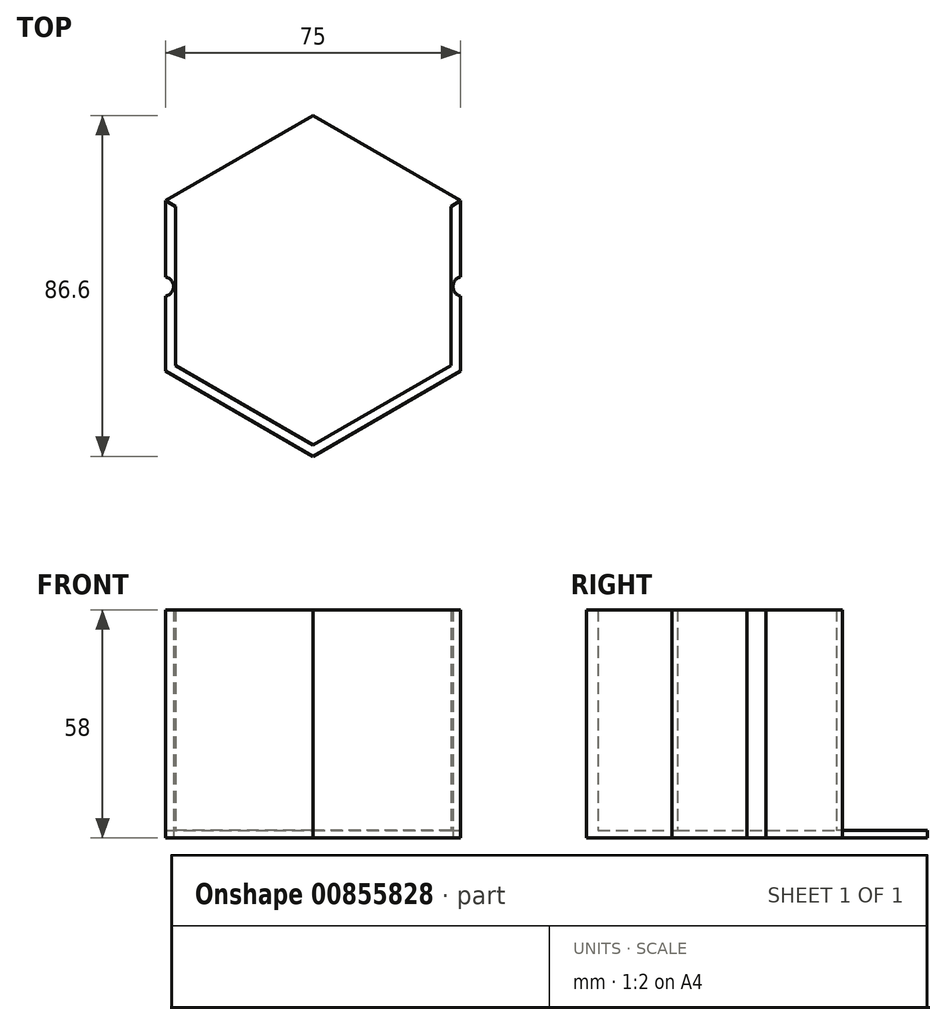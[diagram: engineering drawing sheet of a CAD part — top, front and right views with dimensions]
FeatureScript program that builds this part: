
annotation { "Feature Type Name" : "Feature", "Feature Type Description" : "" }
export const myFeature = defineFeature(function(context is Context, id is Id, definition is map)
    precondition{}
    {
        {
            var Q0;
            Q0=qCreatedBy(makeId("Top.planeOp"),FACE);
            var sketch = newSketch(context, id + "F0", { "sketchPlane" : qUnion([Q0])});
            skCircle(sketch, "E0.cCircle", {"center": v(0, 0) * mm, "radius": 37.5 * mm, "construction": true});
            skLineSegment(sketch, "E0.0", {"start": v(37.5, 21.65) * mm, "end": v(37.5, 2.27) * mm});
            skLineSegment(sketch, "E0.1", {"start": v(37.5, -21.65) * mm, "end": v(0, -43.3) * mm});
            skLineSegment(sketch, "E0.2", {"start": v(0, -43.3) * mm, "end": v(-37.5, -21.65) * mm});
            skLineSegment(sketch, "E0.3", {"start": v(-37.5, -21.65) * mm, "end": v(-37.5, -2.62) * mm});
            skLineSegment(sketch, "E0.4", {"start": v(-37.5, 21.65) * mm, "end": v(0, 43.3) * mm});
            skLineSegment(sketch, "E0.5", {"start": v(0, 43.3) * mm, "end": v(37.5, 21.65) * mm});
            skPoint(sketch, "E0.0.midPoint", {"position": v(37.5, 0) * mm});
            skCircle(sketch, "E1.cCircle", {"center": v(0, 0) * mm, "radius": 35 * mm, "construction": true});
            skLineSegment(sketch, "E1.0", {"start": v(35, 20.2) * mm, "end": v(35, -20.2) * mm});
            skLineSegment(sketch, "E1.1", {"start": v(35, -20.2) * mm, "end": v(0, -40.41) * mm});
            skLineSegment(sketch, "E1.2", {"start": v(0, -40.41) * mm, "end": v(-35, -20.2) * mm});
            skLineSegment(sketch, "E1.3", {"start": v(-35, -20.2) * mm, "end": v(-35, 20.2) * mm});
            skLineSegment(sketch, "E1.4", {"start": v(-35, 20.2) * mm, "end": v(0, 40.41) * mm});
            skLineSegment(sketch, "E1.5", {"start": v(0, 40.41) * mm, "end": v(35, 20.2) * mm});
            skPoint(sketch, "E1.0.midPoint", {"position": v(35, 0) * mm});
            skArc(sketch, "E2", {"start": v(37.5, 2.27) * mm, "mid": v(35.53, -0.17) * mm, "end": v(37.5, -2.6) * mm});
            skArc(sketch, "E3", {"start": v(-37.5, -2.62) * mm, "mid": v(-35.47, -0.17) * mm, "end": v(-37.5, 2.29) * mm});
            skPoint(sketch, "E4.orphan", {"position": v(-37.97, 2.33) * mm});
            skPoint(sketch, "E5.orphan", {"position": v(38.03, 2.33) * mm});
            skLineSegment(sketch, "E6.trimOffspring", {"start": v(-37.5, 2.29) * mm, "end": v(-37.5, 21.65) * mm});
            skLineSegment(sketch, "E7.trimOffspring", {"start": v(37.5, -2.6) * mm, "end": v(37.5, -21.65) * mm});
            skSolve(sketch);
        }
        {
            var Q0;
            Q0=makeQuery(id+"F0.imprint","IMPRINT",FACE,{"disambiguationData":[TD([[makeQuery(id+"F0.imprint","IMPRINT",EDGE,{"derivedFrom":sQuery(id+"F0.wireOp",EDGE,"E1.0")}),-1.0]])]});
            var Q1;
            Q1=makeQuery(id+"F0.imprint","IMPRINT",FACE,{"disambiguationData":[TD([[makeQuery(id+"F0.imprint","IMPRINT",EDGE,{"derivedFrom":sQuery(id+"F0.wireOp",EDGE,"E0.0")}),-1.0]])]});
            extrude(context, id + "F1", {"entities" : qUnion([Q0, Q1]), "depth" : 2 * mm, "offsetDistance" : 25 * mm});
        }
        {
            var Q0;
            Q0=makeQuery(id+"F1.opExtrude","CAP_FACE",FACE,{"disambiguationData":[OSD([sQuery(id+"F0.wireOp",EDGE,"E0.0"),sQuery(id+"F0.wireOp",EDGE,"E0.1"),sQuery(id+"F0.wireOp",EDGE,"E0.2"),sQuery(id+"F0.wireOp",EDGE,"E0.3"),sQuery(id+"F0.wireOp",EDGE,"E0.4"),sQuery(id+"F0.wireOp",EDGE,"E0.5")])],"isStart":false});
            var sketch = newSketch(context, id + "F2", { "sketchPlane" : qUnion([Q0])});
            skLineSegment(sketch, "E8.2", {"start": v(-37.5, -21.65) * mm, "end": v(-37.5, -2.62) * mm});
            skArc(sketch, "E8.3", {"start": v(-37.5, -2.62) * mm, "mid": v(-35.47, -0.17) * mm, "end": v(-37.5, 2.29) * mm});
            skLineSegment(sketch, "E8.4", {"start": v(0, -43.3) * mm, "end": v(-37.5, -21.65) * mm});
            skLineSegment(sketch, "E8.5", {"start": v(37.5, -21.65) * mm, "end": v(0, -43.3) * mm});
            skLineSegment(sketch, "E8.6", {"start": v(37.5, 21.65) * mm, "end": v(37.5, 2.27) * mm});
            skLineSegment(sketch, "E8.9", {"start": v(35, 20.2) * mm, "end": v(35, -20.2) * mm});
            skLineSegment(sketch, "E8.10", {"start": v(35, -20.2) * mm, "end": v(0, -40.41) * mm});
            skLineSegment(sketch, "E8.11", {"start": v(0, -40.41) * mm, "end": v(-35, -20.2) * mm});
            skLineSegment(sketch, "E8.12", {"start": v(-35, -20.2) * mm, "end": v(-35, 20.2) * mm});
            skArc(sketch, "E9.0", {"start": v(37.5, 2.27) * mm, "mid": v(35.53, -0.17) * mm, "end": v(37.5, -2.6) * mm});
            skLineSegment(sketch, "E10", {"start": v(-37.5, 21.65) * mm, "end": v(-35, 20.2) * mm});
            skLineSegment(sketch, "E11", {"start": v(35, 20.2) * mm, "end": v(37.5, 21.65) * mm});
            skSolve(sketch);
        }
        {
            var Q0;
            Q0=makeQuery(id+"F2.imprint","IMPRINT",FACE,{"disambiguationData":[TD([[makeQuery(id+"F2.imprint","IMPRINT",EDGE,{"derivedFrom":sQuery(id+"F2.wireOp",EDGE,"E8.2")}),-1.0]])]});
            extrude(context, id + "F3", {"entities" : qUnion([Q0]), "operationType" : NewBodyOperationType.ADD, "depth" : 56 * mm, "offsetDistance" : 25 * mm});
        }
    });
